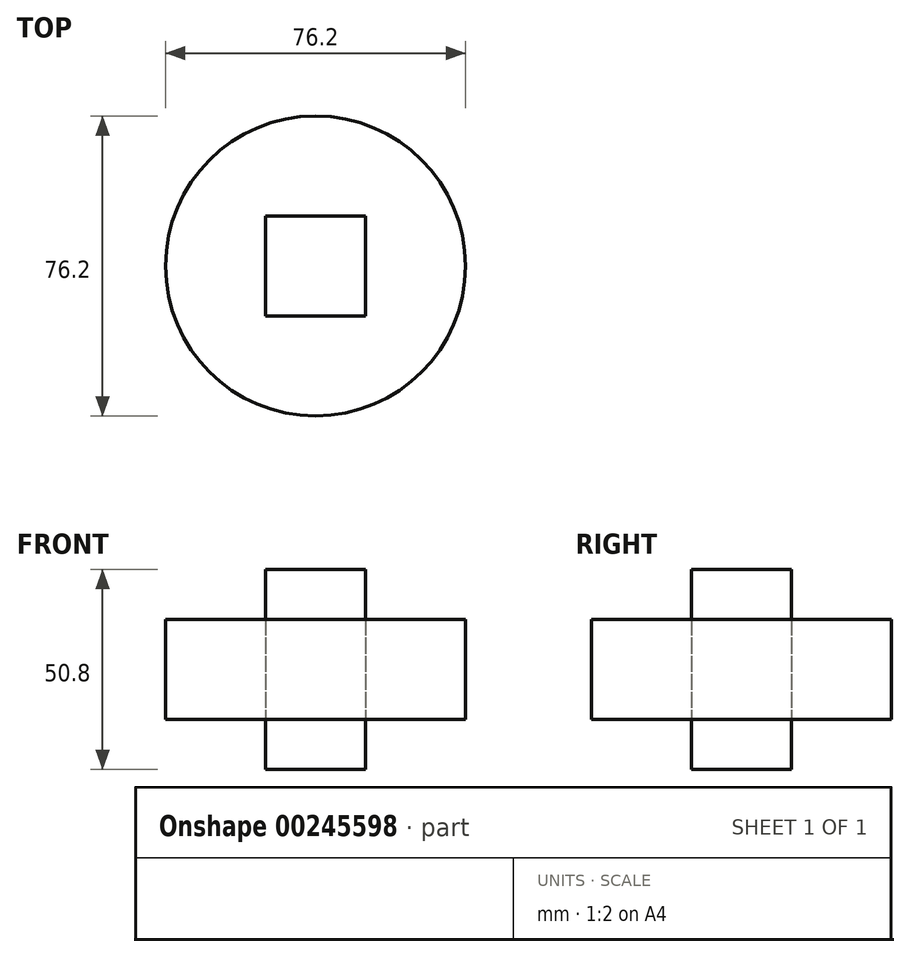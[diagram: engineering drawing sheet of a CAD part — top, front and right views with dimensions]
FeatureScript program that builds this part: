
annotation { "Feature Type Name" : "Feature", "Feature Type Description" : "" }
export const myFeature = defineFeature(function(context is Context, id is Id, definition is map)
    precondition{}
    {
        {
            var Q0;
            Q0=qCreatedBy(makeId("Top.planeOp"),FACE);
            var sketch = newSketch(context, id + "F0", { "sketchPlane" : qUnion([Q0])});
            skCircle(sketch, "E0", {"center": v(0, 0) * mm, "radius": 38.1 * mm});
            skSolve(sketch);
        }
        {
            var Q0;
            Q0=makeQuery(id+"F0.imprint","IMPRINT",FACE,{"disambiguationData":[TD([[makeQuery(id+"F0.imprint","IMPRINT",EDGE,{"derivedFrom":sQuery(id+"F0.wireOp",EDGE,"E0")}),1.0]])]});
            extrude(context, id + "F1", {"entities" : qUnion([Q0]), "endBound" : BoundingType.SYMMETRIC, "depth" : 25.4 * mm});
        }
        {
            var Q0;
            Q0=qCreatedBy(makeId("Top.planeOp"),FACE);
            var sketch = newSketch(context, id + "F2", { "sketchPlane" : qUnion([Q0])});
            skLineSegment(sketch, "E1.bottom", {"start": v(-12.7, 12.7) * mm, "end": v(12.7, 12.7) * mm});
            skLineSegment(sketch, "E1.top", {"start": v(-12.7, -12.7) * mm, "end": v(12.7, -12.7) * mm});
            skLineSegment(sketch, "E1.left", {"start": v(-12.7, 12.7) * mm, "end": v(-12.7, -12.7) * mm});
            skLineSegment(sketch, "E1.right", {"start": v(12.7, 12.7) * mm, "end": v(12.7, -12.7) * mm});
            skPoint(sketch, "E1.middle", {"position": v(0, 0) * mm});
            skSolve(sketch);
        }
        {
            var Q0;
            Q0=makeQuery(id+"F2.imprint","IMPRINT",FACE,{"disambiguationData":[TD([[makeQuery(id+"F2.imprint","IMPRINT",EDGE,{"derivedFrom":sQuery(id+"F2.wireOp",EDGE,"E1.bottom")}),-1.0]])]});
            extrude(context, id + "F3", {"entities" : qUnion([Q0]), "endBound" : BoundingType.SYMMETRIC, "depth" : 50.8 * mm});
        }
        {
            var Q0;
            Q0=makeQuery(id+"F1.opExtrude","SWEPT_BODY",BODY,{"disambiguationData":[OSD([sQuery(id+"F0.wireOp",EDGE,"E0")])]});
            var Q1;
            Q1=makeQuery(id+"F3.opExtrude","SWEPT_BODY",BODY,{"disambiguationData":[OSD([sQuery(id+"F2.wireOp",EDGE,"E1.bottom"),sQuery(id+"F2.wireOp",EDGE,"E1.top"),sQuery(id+"F2.wireOp",EDGE,"E1.left"),sQuery(id+"F2.wireOp",EDGE,"E1.right")])]});
            var Q2;
            Q2=makeQuery(id+"F1.opExtrude","SWEPT_BODY",BODY,{"disambiguationData":[OSD([sQuery(id+"F0.wireOp",EDGE,"E0")])]});
            booleanBodies(context, id + "F4", {"operationType" : BooleanOperationType.INTERSECTION, "tools" : qUnion([Q0, Q1]), "targets" : qUnion([Q2]), "keepTools" : true});
        }
    });
